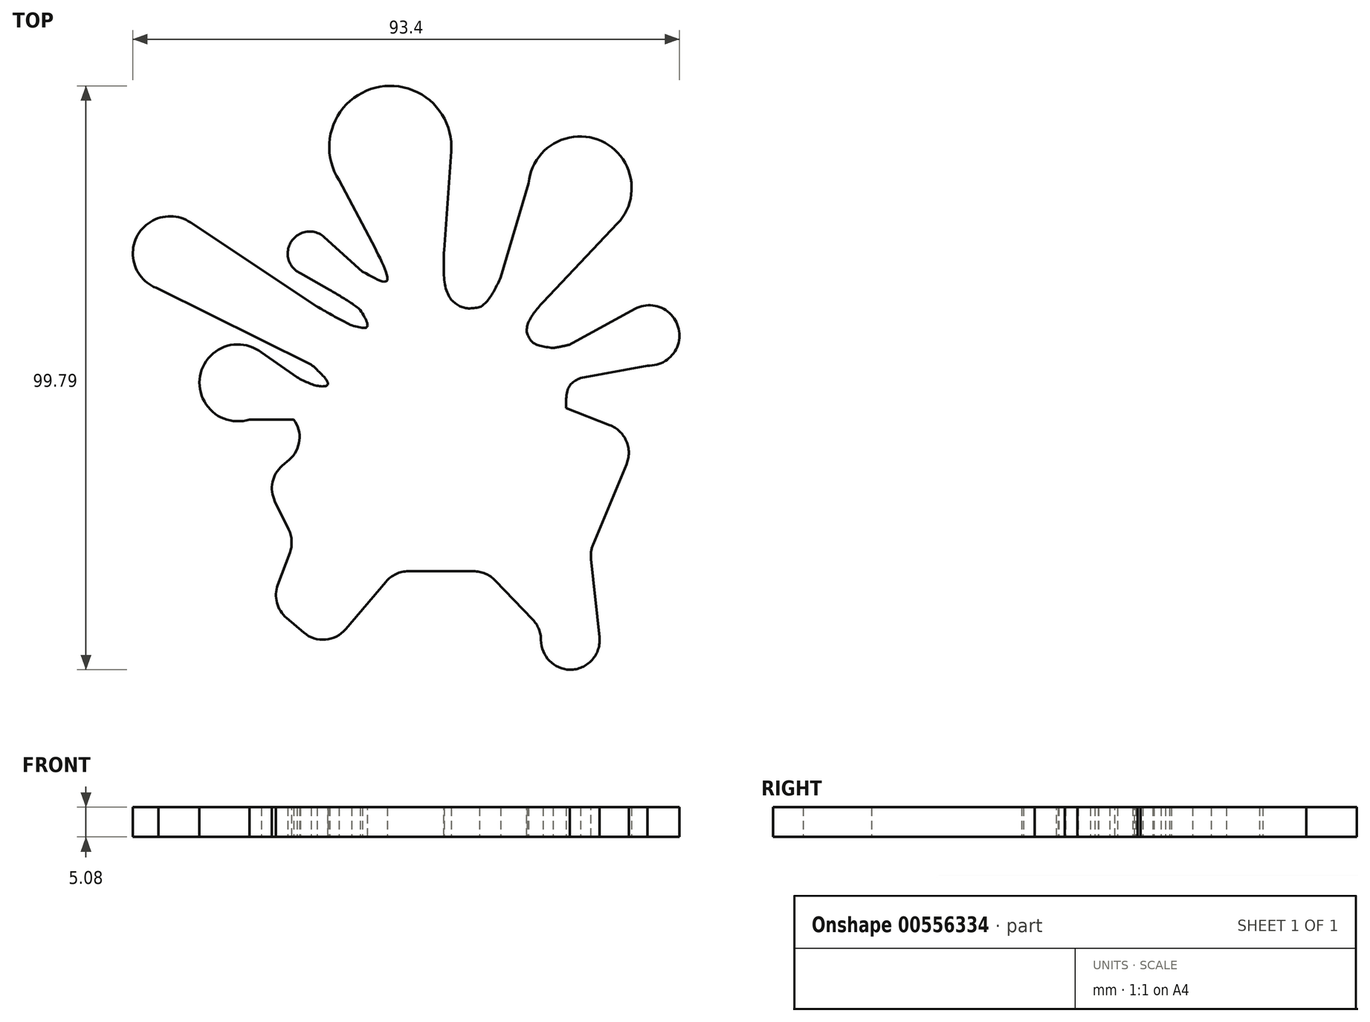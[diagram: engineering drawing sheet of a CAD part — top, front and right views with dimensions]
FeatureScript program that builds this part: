
annotation { "Feature Type Name" : "Feature", "Feature Type Description" : "" }
export const myFeature = defineFeature(function(context is Context, id is Id, definition is map)
    precondition{}
    {
        {
            var Q0;
            Q0=qCreatedBy(makeId("Top.planeOp"),FACE);
            var sketch = newSketch(context, id + "F0", { "sketchPlane" : qUnion([Q0])});
            skCircle(sketch, "E0", {"center": v(0, 0) * mm, "radius": 21.56 * mm});
            skCircle(sketch, "E1", {"center": v(23.42, 42.38) * mm, "radius": 8.83 * mm});
            skCircle(sketch, "E2", {"center": v(35.26, 17.19) * mm, "radius": 5.15 * mm});
            skCircle(sketch, "E3", {"center": v(-22.77, 31.2) * mm, "radius": 3.75 * mm});
            skCircle(sketch, "E4", {"center": v(-8.99, 49.4) * mm, "radius": 10.44 * mm});
            skCircle(sketch, "E5", {"center": v(-35.03, 9.1) * mm, "radius": 6.57 * mm});
            skCircle(sketch, "E6", {"center": v(-46.64, 31.2) * mm, "radius": 6.35 * mm});
            skLineSegment(sketch, "E7", {"start": v(-48.58, 25.16) * mm, "end": v(-18.87, 10.41) * mm});
            skLineSegment(sketch, "E8", {"start": v(-18.87, 10.41) * mm, "end": v(-13.49, 16.81) * mm});
            skLineSegment(sketch, "E9", {"start": v(-13.49, 16.81) * mm, "end": v(-43.13, 36.5) * mm});
            skLineSegment(sketch, "E10", {"start": v(-24.35, 27.8) * mm, "end": v(-9.48, 19.36) * mm});
            skLineSegment(sketch, "E11", {"start": v(-9.48, 19.36) * mm, "end": v(-5.62, 20.8) * mm});
            skLineSegment(sketch, "E12", {"start": v(-5.62, 20.8) * mm, "end": v(-20.27, 33.99) * mm});
            skLineSegment(sketch, "E13", {"start": v(-18.6, 45.31) * mm, "end": v(-5.62, 20.8) * mm});
            skLineSegment(sketch, "E14", {"start": v(1.42, 48.64) * mm, "end": v(-0.56, 21.55) * mm});
            skLineSegment(sketch, "E15", {"start": v(29.83, 36.3) * mm, "end": v(12.23, 17.75) * mm});
            skLineSegment(sketch, "E16", {"start": v(14.64, 43.2) * mm, "end": v(7.78, 20.1) * mm});
            skLineSegment(sketch, "E17", {"start": v(32.79, 21.7) * mm, "end": v(17.08, 13.14) * mm});
            skLineSegment(sketch, "E18", {"start": v(34.94, 12.04) * mm, "end": v(19.5, 9.17) * mm});
            skLineSegment(sketch, "E19", {"start": v(-31.55, 14.66) * mm, "end": v(-20.43, 6.87) * mm});
            skLineSegment(sketch, "E20", {"start": v(-33.03, 2.83) * mm, "end": v(-21.37, 2.83) * mm});
            skPoint(sketch, "E21.0.internal.snap0", {"position": v(21.03, 27.03) * mm});
            skFitSpline(sketch, "E21", {"points": [v(21.03, 15.3) * mm, v(17.08, 13.14) * mm], "startDerivative": vector(-3.94, -2.15) * mm, "endDerivative": vector(-3.94, -2.15) * mm});
            skFitSpline(sketch, "E22", {"points": [v(23.52, 9.92) * mm, v(21.56, 8.44) * mm, v(21.03, 4.74) * mm], "startDerivative": vector(-5.14, -2.54) * mm, "endDerivative": vector(-0.03, -7.64) * mm});
            skFitSpline(sketch, "E23", {"points": [v(21.58, 15.6) * mm, v(17.89, 14.98) * mm, v(15.19, 15.3) * mm], "startDerivative": vector(-7.1, -1.64) * mm, "endDerivative": vector(-5.64, 1.1) * mm});
            skFitSpline(sketch, "E24", {"points": [v(17.08, 22.87) * mm, v(14.37, 18.62) * mm, v(15.19, 15.3) * mm], "startDerivative": vector(-6.8, -7.87) * mm, "endDerivative": vector(3.33, -7.26) * mm});
            skFitSpline(sketch, "E25", {"points": [v(9.86, 27.1) * mm, v(6.94, 22.46) * mm, v(3.57, 21.26) * mm], "startDerivative": vector(-4.66, -9.98) * mm, "endDerivative": vector(-8.05, -1.42) * mm});
            skFitSpline(sketch, "E26", {"points": [v(0.19, 31.74) * mm, v(0.8, 24.34) * mm, v(3.57, 21.26) * mm], "startDerivative": vector(-0.46, -14.57) * mm, "endDerivative": vector(7.61, -5.98) * mm});
            skFitSpline(sketch, "E27", {"points": [v(-12.1, 33.06) * mm, v(-9.61, 26.5) * mm, v(-13.72, 28.1) * mm], "startDerivative": vector(8.32, -16.05) * mm, "endDerivative": vector(-12.35, 7.02) * mm});
            skFitSpline(sketch, "E28", {"points": [v(-19.35, 24.97) * mm, v(-13.2, 20.66) * mm, v(-11.9, 17.97) * mm], "startDerivative": vector(12.07, -7.05) * mm, "endDerivative": vector(2.1, -6.96) * mm});
            skFitSpline(sketch, "E29", {"points": [v(-21.5, 22.13) * mm, v(-14.35, 18.41) * mm, v(-11.9, 17.97) * mm], "startDerivative": vector(12.5, -7.25) * mm, "endDerivative": vector(6.1, -0.41) * mm});
            skFitSpline(sketch, "E30", {"points": [v(-24.93, 10.03) * mm, v(-21.17, 8.52) * mm, v(-19.65, 8.86) * mm, v(-22.5, 12.21) * mm], "startDerivative": vector(10.3, -5.31) * mm, "endDerivative": vector(-11.58, 10.55) * mm});
            skFitSpline(sketch, "E31", {"points": [v(-25.5, 2.83) * mm, v(-22.85, 1.66) * mm, v(-21.56, 0) * mm], "startDerivative": vector(5.48, -1.79) * mm, "endDerivative": vector(2.33, -3.94) * mm});
            skFitSpline(sketch, "E32", {"points": [v(-15.6, 18.92) * mm, v(-12.96, 18.66) * mm, v(-14.12, 21.55) * mm], "startDerivative": vector(7.35, -2.05) * mm, "endDerivative": vector(-4.26, 7.14) * mm});
            skFitSpline(sketch, "E33", {"points": [v(1.44, 23.25) * mm, v(3.59, 21.92) * mm, v(6.4, 22.05) * mm], "startDerivative": vector(4.14, -3.46) * mm, "endDerivative": vector(5.76, 1) * mm});
            skFitSpline(sketch, "E34", {"points": [v(14.37, 17.6) * mm, v(15.48, 15.92) * mm, v(18.83, 15.05) * mm], "startDerivative": vector(1.82, -4.4) * mm, "endDerivative": vector(6.86, -0.84) * mm});
            skLineSegment(sketch, "E35", {"start": v(-21.56, 0) * mm, "end": v(-30.43, -7.62) * mm});
            skLineSegment(sketch, "E36", {"start": v(-30.43, -7.62) * mm, "end": v(-25.4, -17.9) * mm});
            skLineSegment(sketch, "E37", {"start": v(-25.4, -17.9) * mm, "end": v(-29.45, -28.8) * mm});
            skLineSegment(sketch, "E38", {"start": v(-29.45, -28.8) * mm, "end": v(-19.9, -36.89) * mm});
            skLineSegment(sketch, "E39", {"start": v(-19.9, -36.89) * mm, "end": v(-8.24, -23.12) * mm});
            skLineSegment(sketch, "E40", {"start": v(-8.24, -23.12) * mm, "end": v(7.4, -23.12) * mm});
            skLineSegment(sketch, "E41", {"start": v(7.4, -23.12) * mm, "end": v(17.7, -33.83) * mm});
            skLineSegment(sketch, "E42", {"start": v(17.7, -33.83) * mm, "end": v(15, -39.95) * mm});
            skLineSegment(sketch, "E43", {"start": v(15, -39.95) * mm, "end": v(27.37, -39.95) * mm});
            skLineSegment(sketch, "E44", {"start": v(27.37, -39.95) * mm, "end": v(25.16, -19.75) * mm});
            skLineSegment(sketch, "E45", {"start": v(25.16, -19.75) * mm, "end": v(33.37, 0) * mm});
            skLineSegment(sketch, "E46", {"start": v(33.37, 0) * mm, "end": v(21.03, 4.74) * mm});
            skSolve(sketch);
        }
        {
            var Q0;
            Q0 = qSketchRegion(id + "F0", true);
            var Q1;
            {var subQ0=sQuery(id+"F0.wireOp",EDGE,"E8");Q1=makeQuery(id+"F0.imprint","IMPRINT",FACE,{"disambiguationData":[TD([[makeQuery(id+"F0.imprint","IMPRINT",EDGE,{"derivedFrom":subQ0}),1.0]])]});}
            var Q2;
            {var subQ0=sQuery(id+"F0.wireOp",EDGE,"E11");Q2=makeQuery(id+"F0.imprint","IMPRINT",FACE,{"disambiguationData":[TD([[makeQuery(id+"F0.imprint","IMPRINT",EDGE,{"derivedFrom":subQ0}),1.0]])]});}
            extrude(context, id + "F1", {"entities" : qUnion([Q0, Q1, Q2]), "depth" : 5.08 * mm, "offsetDistance" : 25.4 * mm});
        }
        {
            var Q0;
            Q0=makeQuery(id+"F1.opExtrude","SWEPT_EDGE",EDGE,{"disambiguationData":[OSD([sQuery(id+"F0.wireOp",EDGE,"E38"),sQuery(id+"F0.wireOp",EDGE,"E39")])]});
            var Q1;
            Q1=makeQuery(id+"F1.opExtrude","SWEPT_EDGE",EDGE,{"disambiguationData":[OSD([sQuery(id+"F0.wireOp",EDGE,"E39"),sQuery(id+"F0.wireOp",EDGE,"E40")])]});
            var Q2;
            Q2=makeQuery(id+"F1.opExtrude","SWEPT_EDGE",EDGE,{"disambiguationData":[OSD([sQuery(id+"F0.wireOp",EDGE,"E40"),sQuery(id+"F0.wireOp",EDGE,"E41")])]});
            var Q3;
            Q3=makeQuery(id+"F1.opExtrude","SWEPT_EDGE",EDGE,{"disambiguationData":[OSD([sQuery(id+"F0.wireOp",EDGE,"E43"),sQuery(id+"F0.wireOp",EDGE,"E44")])]});
            var Q4;
            Q4=makeQuery(id+"F1.opExtrude","SWEPT_EDGE",EDGE,{"disambiguationData":[OSD([sQuery(id+"F0.wireOp",EDGE,"E44"),sQuery(id+"F0.wireOp",EDGE,"E45")])]});
            var Q5;
            Q5=makeQuery(id+"F1.opExtrude","SWEPT_EDGE",EDGE,{"disambiguationData":[OSD([sQuery(id+"F0.wireOp",EDGE,"E45"),sQuery(id+"F0.wireOp",EDGE,"E46")])]});
            var Q6;
            Q6=makeQuery(id+"F1.opExtrude","SWEPT_EDGE",EDGE,{"disambiguationData":[OSD([sQuery(id+"F0.wireOp",EDGE,"E36"),sQuery(id+"F0.wireOp",EDGE,"E37")])]});
            var Q7;
            Q7=makeQuery(id+"F1.opExtrude","SWEPT_EDGE",EDGE,{"disambiguationData":[OSD([sQuery(id+"F0.wireOp",EDGE,"E37"),sQuery(id+"F0.wireOp",EDGE,"E38")])]});
            var Q8;
            Q8=makeQuery(id+"F1.opExtrude","SWEPT_EDGE",EDGE,{"disambiguationData":[OSD([sQuery(id+"F0.wireOp",EDGE,"E35"),sQuery(id+"F0.wireOp",EDGE,"E36")])]});
            var Q9;
            Q9=makeQuery(id+"F1.opExtrude","SWEPT_EDGE",EDGE,{"disambiguationData":[OSD([sQuery(id+"F0.wireOp",EDGE,"E0"),sQuery(id+"F0.wireOp",EDGE,"E31"),sQuery(id+"F0.wireOp",EDGE,"E35")])]});
            var Q10;
            Q10=makeQuery(id+"F1.opExtrude","SWEPT_EDGE",EDGE,{"disambiguationData":[OSD([sQuery(id+"F0.wireOp",EDGE,"E41"),sQuery(id+"F0.wireOp",EDGE,"E42")])]});
            fillet(context, id + "F2", {"entities" : qUnion([Q0, Q1, Q2, Q3, Q4, Q5, Q6, Q7, Q8, Q9, Q10]), "radius" : 5.08 * mm, "tangentPropagation" : true, "allowEdgeOverflow" : false});
        }
        {
            var Q0;
            Q0=makeQuery(id+"F1.opExtrude","SWEPT_EDGE",EDGE,{"disambiguationData":[OSD([sQuery(id+"F0.wireOp",EDGE,"E42"),sQuery(id+"F0.wireOp",EDGE,"E43")])]});
            fillet(context, id + "F3", {"entities" : qUnion([Q0]), "radius" : 5.08 * mm, "tangentPropagation" : true, "allowEdgeOverflow" : false});
        }
    });
